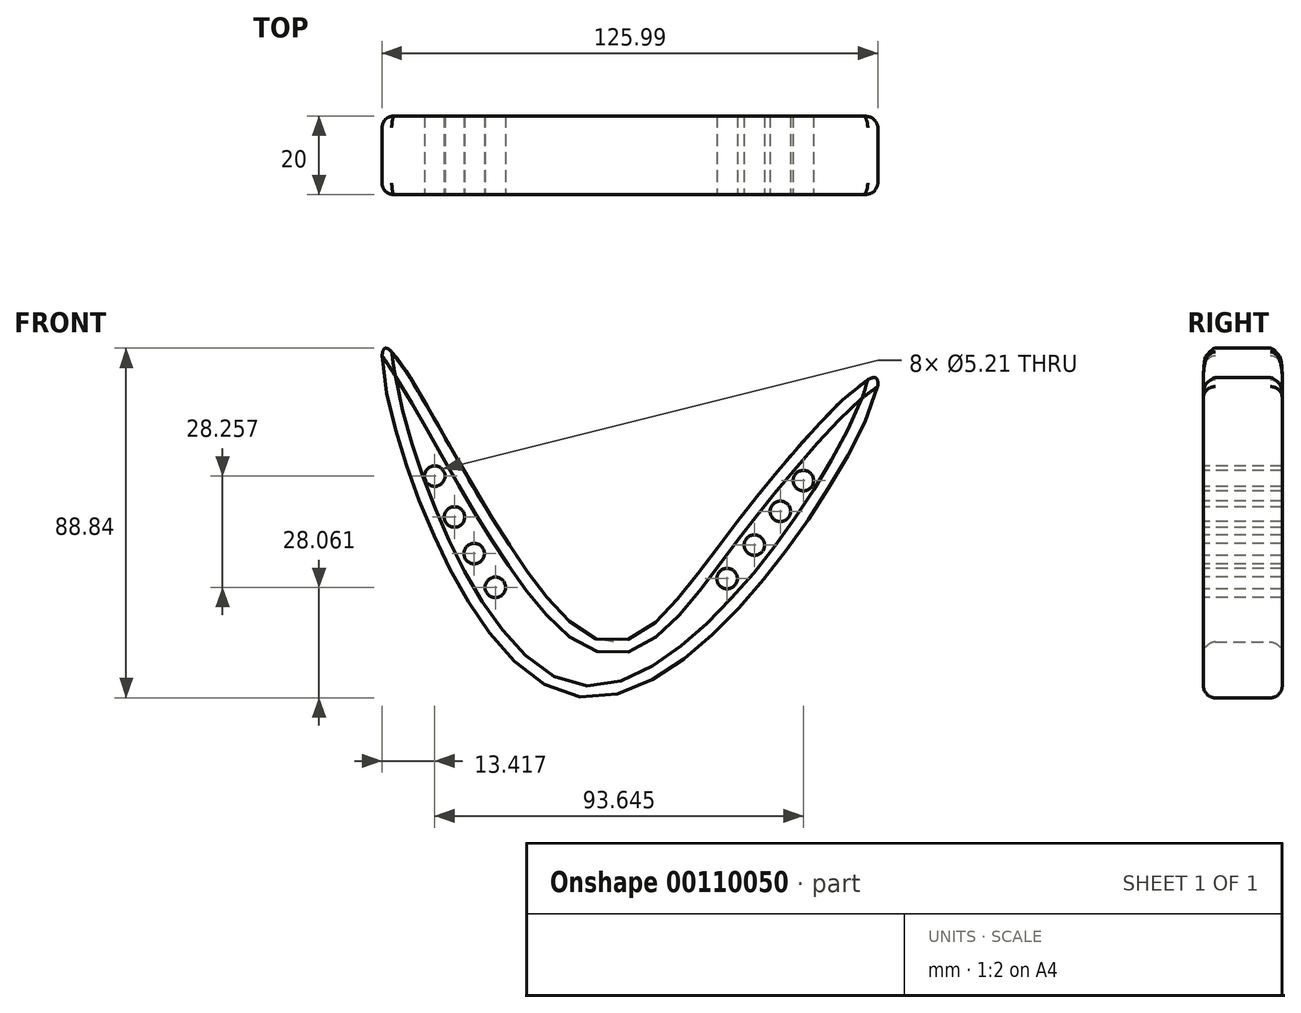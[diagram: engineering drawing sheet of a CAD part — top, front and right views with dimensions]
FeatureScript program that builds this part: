
annotation { "Feature Type Name" : "Feature", "Feature Type Description" : "" }
export const myFeature = defineFeature(function(context is Context, id is Id, definition is map)
    precondition{}
    {
        {
            var Q0;
            Q0=qCreatedBy(makeId("Front.planeOp"),FACE);
            var sketch = newSketch(context, id + "F0", { "sketchPlane" : qUnion([Q0])});
            skFitSpline(sketch, "E0", {"points": [v(-126.06, 7.68) * mm, v(-202.6, -72.13) * mm, v(-251.45, 16.27) * mm, v(-201.36, -55.45) * mm, v(-163.3, -29.6) * mm, v(-126.06, 7.68) * mm]});
            skSolve(sketch);
        }
        {
            var Q0;
            Q0 = qSketchRegion(id + "F0", true);
            var Q1;
            Q1=sQuery(id+"F0.wireOp",EDGE,"E0");
            extrude(context, id + "F1", {"entities" : qUnion([Q0]), "surfaceEntities" : qUnion([Q1]), "endBound" : BoundingType.SYMMETRIC, "depth" : 20 * mm});
        }
        {
            var Q0;
            Q0=makeQuery(id+"F1.opExtrude","CAP_EDGE",EDGE,{"disambiguationData":[OSD([sQuery(id+"F0.wireOp",EDGE,"E0")])],"isStart":true});
            var Q1;
            Q1=makeQuery(id+"F1.opExtrude","CAP_EDGE",EDGE,{"disambiguationData":[OSD([sQuery(id+"F0.wireOp",EDGE,"E0")])],"isStart":false});
            fillet(context, id + "F2", {"entities" : qUnion([Q0, Q1]), "radius" : 3 * mm, "tangentPropagation" : true, "allowEdgeOverflow" : false});
        }
        {
            var Q0;
            Q0=makeQuery(id+"F1.opExtrude","CAP_FACE",FACE,{"disambiguationData":[OSD([sQuery(id+"F0.wireOp",EDGE,"E0")])],"isStart":false});
            var sketch = newSketch(context, id + "F3", { "sketchPlane" : qUnion([Q0])});
            skCircle(sketch, "E1", {"center": v(-233.62, -26.48) * mm, "radius": 2.6 * mm});
            skCircle(sketch, "E2", {"center": v(-238.63, -16.11) * mm, "radius": 2.6 * mm});
            skCircle(sketch, "E3", {"center": v(-228.62, -35.78) * mm, "radius": 2.6 * mm});
            skCircle(sketch, "E4", {"center": v(-223.25, -44.37) * mm, "radius": 2.6 * mm});
            skCircle(sketch, "E5", {"center": v(-144.99, -17.23) * mm, "radius": 2.6 * mm});
            skCircle(sketch, "E6", {"center": v(-150.85, -25.03) * mm, "radius": 2.6 * mm});
            skCircle(sketch, "E7", {"center": v(-157.45, -33.63) * mm, "radius": 2.6 * mm});
            skCircle(sketch, "E8", {"center": v(-164.37, -42.15) * mm, "radius": 2.6 * mm});
            skSolve(sketch);
        }
        {
            var Q0;
            Q0=makeQuery(id+"F3.imprint","IMPRINT",FACE,{"disambiguationData":[TD([[makeQuery(id+"F3.imprint","IMPRINT",EDGE,{"derivedFrom":sQuery(id+"F3.wireOp",EDGE,"E1")}),1.0]])]});
            var Q1;
            Q1=makeQuery(id+"F3.imprint","IMPRINT",FACE,{"disambiguationData":[TD([[makeQuery(id+"F3.imprint","IMPRINT",EDGE,{"derivedFrom":sQuery(id+"F3.wireOp",EDGE,"E5")}),1.0]])]});
            var Q2;
            Q2=makeQuery(id+"F3.imprint","IMPRINT",FACE,{"disambiguationData":[TD([[makeQuery(id+"F3.imprint","IMPRINT",EDGE,{"derivedFrom":sQuery(id+"F3.wireOp",EDGE,"E6")}),1.0]])]});
            var Q3;
            Q3=makeQuery(id+"F3.imprint","IMPRINT",FACE,{"disambiguationData":[TD([[makeQuery(id+"F3.imprint","IMPRINT",EDGE,{"derivedFrom":sQuery(id+"F3.wireOp",EDGE,"E7")}),1.0]])]});
            var Q4;
            Q4=makeQuery(id+"F3.imprint","IMPRINT",FACE,{"disambiguationData":[TD([[makeQuery(id+"F3.imprint","IMPRINT",EDGE,{"derivedFrom":sQuery(id+"F3.wireOp",EDGE,"E2")}),1.0]])]});
            var Q5;
            Q5=makeQuery(id+"F3.imprint","IMPRINT",FACE,{"disambiguationData":[TD([[makeQuery(id+"F3.imprint","IMPRINT",EDGE,{"derivedFrom":sQuery(id+"F3.wireOp",EDGE,"E3")}),1.0]])]});
            var Q6;
            Q6=makeQuery(id+"F3.imprint","IMPRINT",FACE,{"disambiguationData":[TD([[makeQuery(id+"F3.imprint","IMPRINT",EDGE,{"derivedFrom":sQuery(id+"F3.wireOp",EDGE,"E4")}),1.0]])]});
            var Q7;
            Q7=makeQuery(id+"F3.imprint","IMPRINT",FACE,{"disambiguationData":[TD([[makeQuery(id+"F3.imprint","IMPRINT",EDGE,{"derivedFrom":sQuery(id+"F3.wireOp",EDGE,"E8")}),1.0]])]});
            var Q8;
            Q8=sQuery(id+"F3.wireOp",EDGE,"E5");
            var Q9;
            Q9=sQuery(id+"F3.wireOp",EDGE,"E6");
            var Q10;
            Q10=sQuery(id+"F3.wireOp",EDGE,"E8");
            var Q11;
            Q11=sQuery(id+"F3.wireOp",EDGE,"E7");
            var Q12;
            Q12=sQuery(id+"F3.wireOp",EDGE,"E4");
            var Q13;
            Q13=sQuery(id+"F3.wireOp",EDGE,"E3");
            var Q14;
            Q14=sQuery(id+"F3.wireOp",EDGE,"E2");
            var Q15;
            Q15=sQuery(id+"F3.wireOp",EDGE,"E1");
            extrude(context, id + "F4", {"entities" : qUnion([Q0, Q1, Q2, Q3, Q4, Q5, Q6, Q7]), "operationType" : NewBodyOperationType.REMOVE, "surfaceEntities" : qUnion([Q8, Q9, Q10, Q11, Q12, Q13, Q14, Q15]), "endBound" : BoundingType.THROUGH_ALL, "oppositeDirection" : true, "depth" : 25 * mm});
        }
    });
